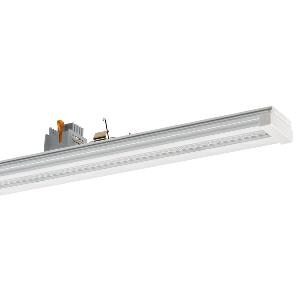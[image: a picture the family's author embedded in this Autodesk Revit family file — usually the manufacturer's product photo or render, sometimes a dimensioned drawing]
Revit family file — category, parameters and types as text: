
# Revit family: conveo_-_cvg_4500_850_w-l_da_7_226848269-00804965_9cd0
name_source: partatom
category: Lighting Fixtures
units: mm (PartAtom-declared; Revit-internal decimal feet)

## family parameters
Cut with Voids When Loaded = No
Host = Face
Light Source = No
Part Type = Normal
Room Calculation Point = No
Round Connector Dimension = Use Diameter
Shared = No

## types (1)
- CONVEO - CVG 4500/850/W-L/DA/7 (1 x LED, 4450 lm, 5000K)
    Apparent Load = 24 VA
    Approval mark = CE
    CIE Flux Codes = 85 97 99 100 100
    Color Rendering = 80-89
    Color Temperature = 5000K
    Control Gear = Electronic ballast
    Default Elevation = 1800 mm
    Description = CVG 4500/850/W-L/DA/7|Continuous-row system|light source: LED|work equipment: Adjustable electronic ballast, digital DALI|connected load: 220-240 V, 50-60 Hz|Power consumption: approx. 24 W|luminous flux: 4450 lm|luminous efficacy: 185 lm/W|colour temperature: Cold white, ca. 5000 K|color rendering index (CRI): >= 80|chromaticity tolerance:  3 SDCM|System of protection: IP 54|class of protection: I|technology: Continuously dimmable|luminaire body|material: Aluminium|surface: Powder coatet|colour: White|lamp cover: Acrylic (PMMA), Satine|weight (net): approx. 1.9 kg|Fastening: Available separately|maximum ambient temperature: 50 ░C|glare control: Lens optics|Approval mark: VDE - ENEC|
    Frequency = 50 Hz
    Height = 70 mm
    Lamp = 1 x LED
    Lamp Light Flux = 4450 lm
    Lamp count = 1
    Length = 1500 mm
    Luminous efficacy = 185 lm/W
    Manufacturer = Waldmann
    ModVariant = No
    Model = 226848269-00804965
    Mounting Place = Ceiling
    Mounting Type = Pendant
    Number of Poles = 1
    OnlyDefault = Yes
    Power Factor = 1
    Product Name = CONVEO - CVG 4500/850/W-L/DA/7
    Product group = Continuous-row system (industry)
    ProductGroupID = 301
    Protection Class = Protection class I
    Protection Degree = IP 54
    RLX_Detail_Level = 1
    RlxData = <blob elided: 99841 chars, md5=89931445>
    Socket = socket
    Standby Power = 0 W
    System Light Flux = 4450 lm
    System Power = 24 W
    Type Comments = Product without accessories
    Type Image = 226848259-00804964_1l7.jpg
    URL = http://relux.com
    VarID = ---
    Voltage = 230 V
    Voltage Range = 220-240 V
    Weight = 0.00 kg
    Width = 64 mm

## geometry (parser evidence)
native form markers: Blend x4, Sweep x9
no freeform markers — native parametric forms only
